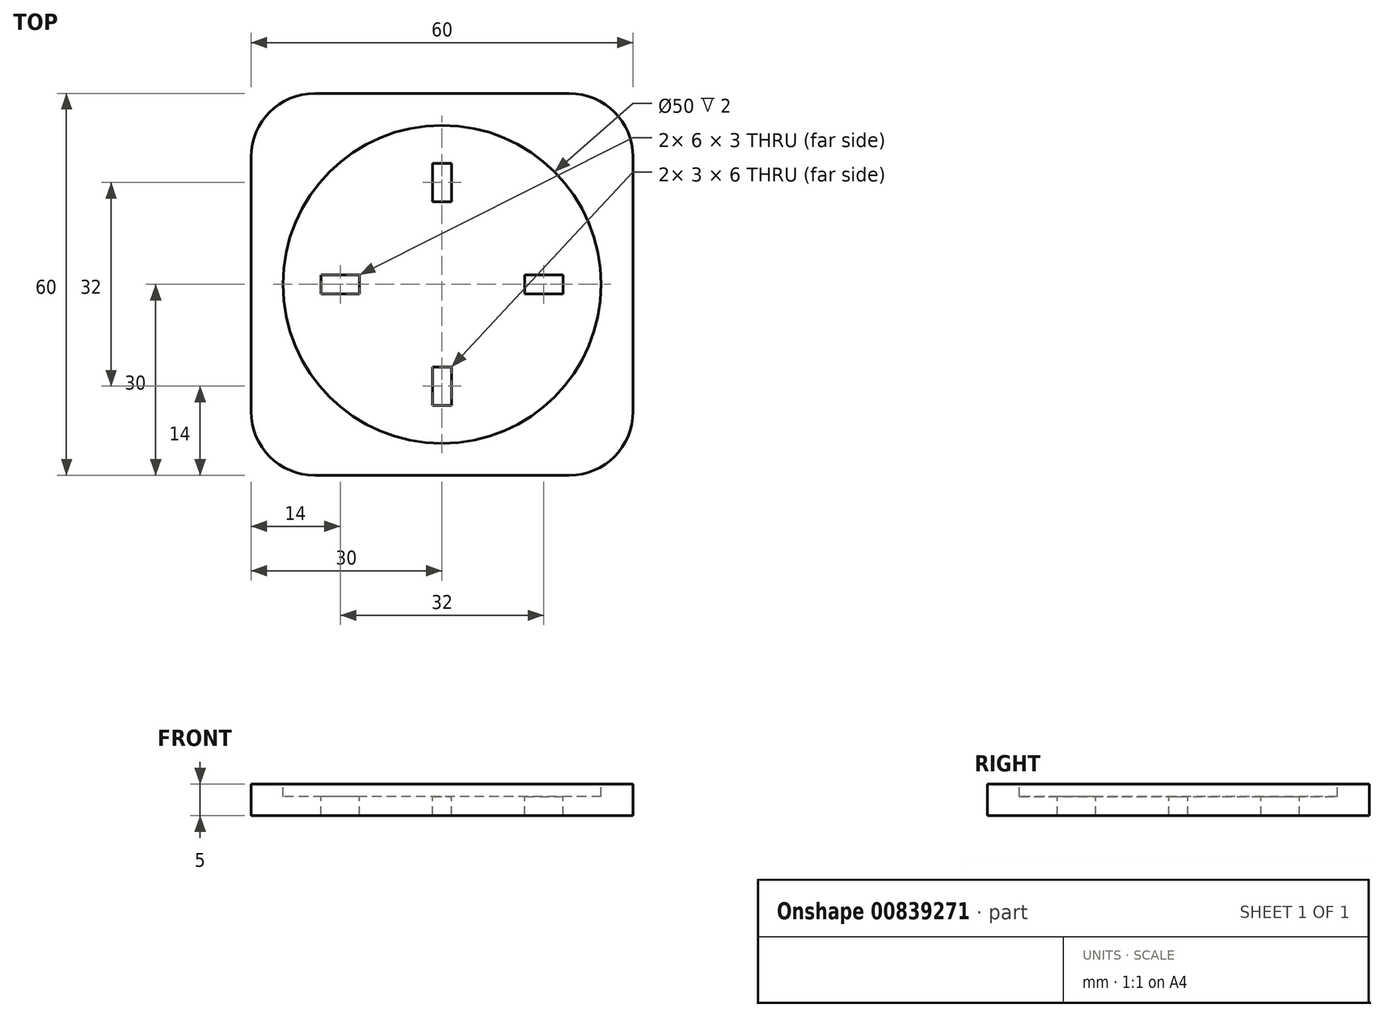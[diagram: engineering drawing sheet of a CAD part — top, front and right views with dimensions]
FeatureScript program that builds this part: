
annotation { "Feature Type Name" : "Feature", "Feature Type Description" : "" }
export const myFeature = defineFeature(function(context is Context, id is Id, definition is map)
    precondition{}
    {
        {
            var Q0;
            Q0=qCreatedBy(makeId("Top.planeOp"),FACE);
            var sketch = newSketch(context, id + "F0", { "sketchPlane" : qUnion([Q0])});
            skLineSegment(sketch, "E0.bottom", {"start": v(30, -30) * mm, "end": v(-30, -30) * mm});
            skLineSegment(sketch, "E0.top", {"start": v(30, 30) * mm, "end": v(-30, 30) * mm});
            skLineSegment(sketch, "E0.left", {"start": v(30, -30) * mm, "end": v(30, 30) * mm});
            skLineSegment(sketch, "E0.right", {"start": v(-30, -30) * mm, "end": v(-30, 30) * mm});
            skPoint(sketch, "E0.middle", {"position": v(0, 0) * mm});
            skSolve(sketch);
        }
        {
            var Q0;
            Q0=makeQuery(id+"F0.imprint","IMPRINT",FACE,{"disambiguationData":[TD([[makeQuery(id+"F0.imprint","IMPRINT",EDGE,{"derivedFrom":sQuery(id+"F0.wireOp",EDGE,"E0.bottom")}),-1.0]])]});
            extrude(context, id + "F1", {"entities" : qUnion([Q0]), "depth" : 5 * mm, "offsetDistance" : 25 * mm});
        }
        {
            var Q0;
            Q0=makeQuery(id+"F1.opExtrude","CAP_FACE",FACE,{"disambiguationData":[OSD([sQuery(id+"F0.wireOp",EDGE,"E0.bottom"),sQuery(id+"F0.wireOp",EDGE,"E0.top"),sQuery(id+"F0.wireOp",EDGE,"E0.left"),sQuery(id+"F0.wireOp",EDGE,"E0.right")])],"isStart":false});
            var sketch = newSketch(context, id + "F2", { "sketchPlane" : qUnion([Q0])});
            skCircle(sketch, "E1", {"center": v(0, 0) * mm, "radius": 25 * mm});
            skSolve(sketch);
        }
        {
            var Q0;
            Q0=makeQuery(id+"F2.imprint","IMPRINT",FACE,{"disambiguationData":[TD([[makeQuery(id+"F2.imprint","IMPRINT",EDGE,{"derivedFrom":sQuery(id+"F2.wireOp",EDGE,"E1")}),1.0]])]});
            extrude(context, id + "F3", {"entities" : qUnion([Q0]), "operationType" : NewBodyOperationType.REMOVE, "oppositeDirection" : true, "depth" : 2 * mm, "offsetDistance" : 25 * mm});
        }
        {
            var Q0;
            Q0=makeQuery(id+"F1.opExtrude","SWEPT_EDGE",EDGE,{"disambiguationData":[OSD([sQuery(id+"F0.wireOp",EDGE,"E0.top"),sQuery(id+"F0.wireOp",EDGE,"E0.right")])]});
            var Q1;
            Q1=makeQuery(id+"F1.opExtrude","SWEPT_EDGE",EDGE,{"disambiguationData":[OSD([sQuery(id+"F0.wireOp",EDGE,"E0.top"),sQuery(id+"F0.wireOp",EDGE,"E0.left")])]});
            var Q2;
            Q2=makeQuery(id+"F1.opExtrude","SWEPT_EDGE",EDGE,{"disambiguationData":[OSD([sQuery(id+"F0.wireOp",EDGE,"E0.bottom"),sQuery(id+"F0.wireOp",EDGE,"E0.right")])]});
            var Q3;
            Q3=makeQuery(id+"F1.opExtrude","SWEPT_EDGE",EDGE,{"disambiguationData":[OSD([sQuery(id+"F0.wireOp",EDGE,"E0.bottom"),sQuery(id+"F0.wireOp",EDGE,"E0.left")])]});
            fillet(context, id + "F4", {"entities" : qUnion([Q0, Q1, Q2, Q3]), "radius" : 10 * mm, "tangentPropagation" : true, "allowEdgeOverflow" : false});
        }
        {
            var Q0;
            Q0=makeQuery(id+"F3.boolean.opBoolean","COPY",FACE,{"derivedFrom":makeQuery(id+"F3.opExtrude","CAP_FACE",FACE,{"disambiguationData":[OSD([sQuery(id+"F2.wireOp",EDGE,"E1")])],"isStart":false})});
            var sketch = newSketch(context, id + "F5", { "sketchPlane" : qUnion([Q0])});
            skLineSegment(sketch, "E2.bottom", {"start": v(1.5, 13) * mm, "end": v(-1.5, 13) * mm});
            skLineSegment(sketch, "E2.top", {"start": v(1.5, 19) * mm, "end": v(-1.5, 19) * mm});
            skLineSegment(sketch, "E2.left", {"start": v(1.5, 13) * mm, "end": v(1.5, 19) * mm});
            skLineSegment(sketch, "E2.right", {"start": v(-1.5, 13) * mm, "end": v(-1.5, 19) * mm});
            skPoint(sketch, "E2.middle", {"position": v(0, 16) * mm});
            skLineSegment(sketch, "E3.1.0", {"start": v(-13, -1.5) * mm, "end": v(-19, -1.5) * mm});
            skLineSegment(sketch, "E3.1.1", {"start": v(-19, 1.5) * mm, "end": v(-19, -1.5) * mm});
            skLineSegment(sketch, "E3.1.2", {"start": v(-13, 1.5) * mm, "end": v(-19, 1.5) * mm});
            skLineSegment(sketch, "E3.1.3", {"start": v(-13, 1.5) * mm, "end": v(-13, -1.5) * mm});
            skLineSegment(sketch, "E3.2.0", {"start": v(1.5, -13) * mm, "end": v(1.5, -19) * mm});
            skLineSegment(sketch, "E3.2.1", {"start": v(-1.5, -19) * mm, "end": v(1.5, -19) * mm});
            skLineSegment(sketch, "E3.2.2", {"start": v(-1.5, -13) * mm, "end": v(-1.5, -19) * mm});
            skLineSegment(sketch, "E3.2.3", {"start": v(-1.5, -13) * mm, "end": v(1.5, -13) * mm});
            skLineSegment(sketch, "E3.3.0", {"start": v(13, 1.5) * mm, "end": v(19, 1.5) * mm});
            skLineSegment(sketch, "E3.3.1", {"start": v(19, -1.5) * mm, "end": v(19, 1.5) * mm});
            skLineSegment(sketch, "E3.3.2", {"start": v(13, -1.5) * mm, "end": v(19, -1.5) * mm});
            skLineSegment(sketch, "E3.3.3", {"start": v(13, -1.5) * mm, "end": v(13, 1.5) * mm});
            skPoint(sketch, "E3.center", {"position": v(0, 0) * mm});
            skSolve(sketch);
        }
        {
            var Q0;
            Q0 = qSketchRegion(id + "F5", true);
            extrude(context, id + "F6", {"entities" : qUnion([Q0]), "operationType" : NewBodyOperationType.REMOVE, "endBound" : BoundingType.THROUGH_ALL, "oppositeDirection" : true, "depth" : 25 * mm, "offsetDistance" : 25 * mm});
        }
    });
